# Revit family: for update_47070CHN_new
name_source: partatom
category: Plumbing Fixtures
revit_build: Autodesk Revit 2018 (Build: 20170223_1515(x64)
units: mm (PartAtom-declared; Revit-internal decimal feet)

## family parameters
Cut with Voids When Loaded = Yes
Host = Face
OmniClass Number = 23.31.11.00
OmniClass Title = Faucets
Part Type = Normal
Room Calculation Point = No
Round Connector Dimension = Use Diameter
Shared = No

## types (2) — shared parameters
Always visible = Yes
BIMobject category = Taps & Mixers
Connector Description = Water Inlet 9.5 mm
Default Elevation = 1219 mm
Description = AXOR MyEdition 3-hole basin mixer 110 with push-open waste set
Design country = Germany
Diameter = 10 mm  [stored 0.0328084 ft]
EAN code = 4059625450581
Edition number = 1
IFC Classification = Valve
Manufacturer = AXOR
Manufacturer country = Germany
Manufacturer name = AXOR
Masterformat 2014 Code = 22 41 39
Masterformat 2014 Description = Residential Faucets, Supplies, and Trim
Material = AXOR - Metal - 007 Chrome
Model = 47070CHN
OmniClass Code = 23-31 11 00
OmniClass Description = Faucets
Product Guid = 334637da-ebe1-4f49-8e11-51e540ac9014
Product SKU = 47070CHN
Product data url = https://bimobject.com
Product family = AXOR MyEdition
Product group = Basin mixers
Product name = AXOR MyEdition 3-hole basin mixer 110 with push-open waste set
Product url = https://www.axor-design.com
QR code = https://bimobject.com
UNSPSC Code = 301815
URL = https://www.axor-design.com
Uniclass 2015 Code = Pr_40_20_87
Uniclass 2015 Name = Taps and water supply outlet fittings
Uniformat II Code = D2010
Uniformat II Description = Plumbing Fixtures
Version = 1
Weight Net (Kg) = 3,1

## per-type parameters (varying)
| type | Material 1 |
| Chrome/Black Glass | AXOR - Glass - Black Glass |
| Chrome/Mirror Glass | AXOR - Glass - Mirror Glass |

note: [stored X ft] marks values corroborated as IEEE doubles in the binary element streams (Revit-internal decimal feet)

## geometry (parser evidence)
native form markers: Sweep x2
no freeform markers — native parametric forms only
